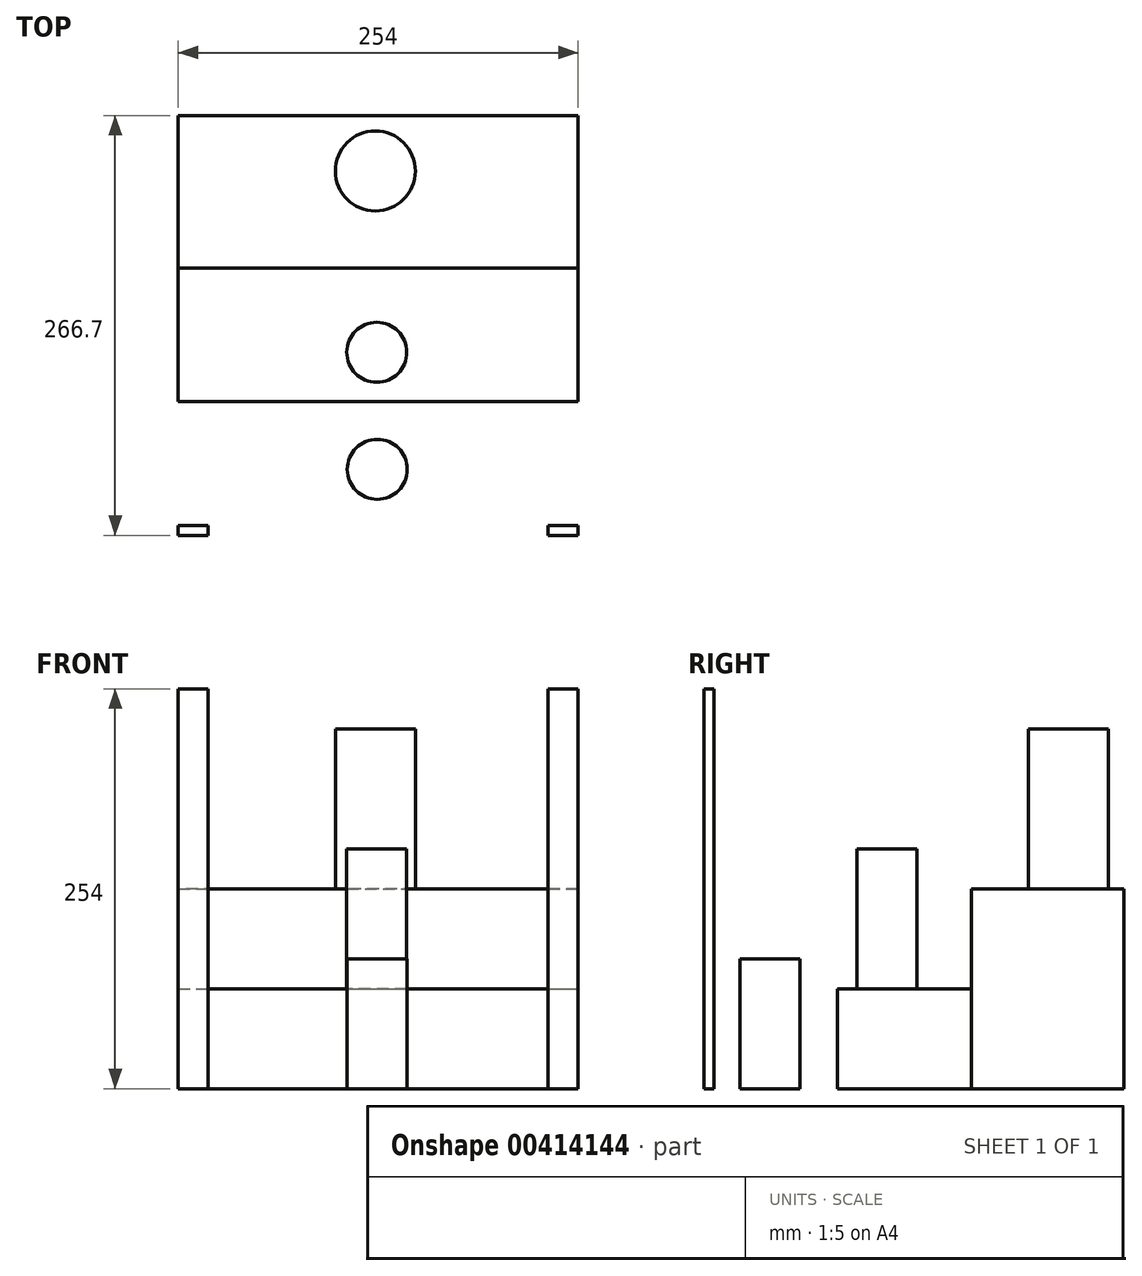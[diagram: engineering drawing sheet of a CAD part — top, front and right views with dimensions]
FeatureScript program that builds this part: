
annotation { "Feature Type Name" : "Feature", "Feature Type Description" : "" }
export const myFeature = defineFeature(function(context is Context, id is Id, definition is map)
    precondition{}
    {
        {
            var Q0;
            Q0=qCreatedBy(makeId("Front.planeOp"),FACE);
            cPlane(context, id + "F0", {"entities" : qUnion([Q0]), "cplaneType" : CPlaneType.OFFSET, "offset" : 266.7 * mm, "oppositeDirection" : true, "width" : 152.4 * mm, "height" : 152.4 * mm});
        }
        {
            var Q0;
            Q0=qCreatedBy(makeId("Right.planeOp"),FACE);
            cPlane(context, id + "F1", {"entities" : qUnion([Q0]), "cplaneType" : CPlaneType.OFFSET, "offset" : 254 * mm, "oppositeDirection" : true, "width" : 152.4 * mm, "height" : 152.4 * mm});
        }
        {
            var Q0;
            Q0=qCreatedBy(makeId("Top.planeOp"),FACE);
            cPlane(context, id + "F2", {"entities" : qUnion([Q0]), "cplaneType" : CPlaneType.OFFSET, "offset" : 254 * mm, "width" : 152.4 * mm, "height" : 152.4 * mm});
        }
        {
            var Q0;
            Q0=qCreatedBy(makeId("Front.planeOp"),FACE);
            var sketch = newSketch(context, id + "F3", { "sketchPlane" : qUnion([Q0])});
            skLineSegment(sketch, "E0", {"start": v(-254, 254) * mm, "end": v(-254, 0) * mm});
            skLineSegment(sketch, "E1", {"start": v(0, 254) * mm, "end": v(0, 0) * mm});
            skLineSegment(sketch, "E2", {"start": v(-254, 254) * mm, "end": v(0, 254) * mm});
            skLineSegment(sketch, "E3", {"start": v(-254, 0) * mm, "end": v(0, 0) * mm});
            skSolve(sketch);
        }
        {
            var Q0;
            Q0=makeQuery(id+"F3.imprint","IMPRINT",FACE,{"disambiguationData":[TD([[makeQuery(id+"F3.imprint","IMPRINT",EDGE,{"derivedFrom":sQuery(id+"F3.wireOp",EDGE,"E0")}),1.0]])]});
            var Q1;
            Q1=sQuery(id+"F3.wireOp",EDGE,"E1");
            var Q2;
            Q2=sQuery(id+"F3.wireOp",EDGE,"E2");
            var Q3;
            Q3=sQuery(id+"F3.wireOp",EDGE,"E0");
            var Q4;
            Q4=sQuery(id+"F3.wireOp",EDGE,"E3");
            var Q5;
            Q5=qCreatedBy(id+"F0.planeOp",FACE);
            extrude(context, id + "F4", {"entities" : qUnion([Q0]), "bodyType" : ToolBodyType.SURFACE, "surfaceEntities" : qUnion([Q1, Q2, Q3, Q4]), "endBound" : BoundingType.UP_TO_SURFACE, "oppositeDirection" : true, "endBoundEntityFace" : qUnion([Q5]), "depth" : 25.4 * mm});
        }
        {
            var Q0;
            Q0=qCreatedBy(makeId("Front.planeOp"),FACE);
            var sketch = newSketch(context, id + "F5", { "sketchPlane" : qUnion([Q0])});
            skLineSegment(sketch, "E4", {"start": v(-234.95, 254) * mm, "end": v(-234.95, 0) * mm});
            skLineSegment(sketch, "E5", {"start": v(-19.05, 254) * mm, "end": v(-19.05, 0) * mm});
            skLineSegment(sketch, "E6", {"start": v(-234.95, 254) * mm, "end": v(-254, 254) * mm});
            skLineSegment(sketch, "E7", {"start": v(-254, 254) * mm, "end": v(-254, 0) * mm});
            skLineSegment(sketch, "E8", {"start": v(-254, 0) * mm, "end": v(-234.95, 0) * mm});
            skLineSegment(sketch, "E9", {"start": v(-19.05, 254) * mm, "end": v(0, 254) * mm});
            skLineSegment(sketch, "E10", {"start": v(0, 254) * mm, "end": v(0, 0) * mm});
            skLineSegment(sketch, "E11", {"start": v(0, 0) * mm, "end": v(-19.05, 0) * mm});
            skSolve(sketch);
        }
        {
            var Q0;
            Q0=makeQuery(id+"F5.imprint","IMPRINT",FACE,{"disambiguationData":[TD([[makeQuery(id+"F5.imprint","IMPRINT",EDGE,{"derivedFrom":sQuery(id+"F5.wireOp",EDGE,"E4")}),-1.0]])]});
            var Q1;
            Q1=makeQuery(id+"F5.imprint","IMPRINT",FACE,{"disambiguationData":[TD([[makeQuery(id+"F5.imprint","IMPRINT",EDGE,{"derivedFrom":sQuery(id+"F5.wireOp",EDGE,"E5")}),1.0]])]});
            extrude(context, id + "F6", {"entities" : qUnion([Q0, Q1]), "oppositeDirection" : true, "depth" : 6.35 * mm});
        }
        {
            var Q0;
            Q0=makeQuery(id+"F4.opExtrude","SWEPT_FACE",FACE,{"disambiguationData":[OSD([sQuery(id+"F3.wireOp",EDGE,"E3")])]});
            var sketch = newSketch(context, id + "F7", { "sketchPlane" : qUnion([Q0])});
            skLineSegment(sketch, "E12", {"start": v(-254, 0) * mm, "end": v(0, 0) * mm});
            skLineSegment(sketch, "E13.1.0.0", {"start": v(-254, -84.84) * mm, "end": v(0, -84.84) * mm});
            skLineSegment(sketch, "E13.2.0.0", {"start": v(-254, -169.67) * mm, "end": v(0, -169.67) * mm});
            skLineSegment(sketch, "E13.direction1", {"start": v(-254, 0) * mm, "end": v(-254, -84.84) * mm, "construction": true});
            skLineSegment(sketch, "E14", {"start": v(-254, 0) * mm, "end": v(-254, -266.7) * mm});
            skLineSegment(sketch, "E15", {"start": v(-254, -266.7) * mm, "end": v(0, -266.7) * mm});
            skLineSegment(sketch, "E16", {"start": v(0, -266.7) * mm, "end": v(0, 0) * mm});
            skSolve(sketch);
        }
        {
            var Q0;
            {var subQ0=sQuery(id+"F7.wireOp",EDGE,"E13.1.0.0");Q0=makeQuery(id+"F7.imprint","IMPRINT",FACE,{"disambiguationData":[TD([[makeQuery(id+"F7.imprint","IMPRINT",EDGE,{"derivedFrom":subQ0}),-1.0]])]});}
            extrude(context, id + "F8", {"entities" : qUnion([Q0]), "oppositeDirection" : true, "depth" : 63.5 * mm});
        }
        {
            var Q0;
            {var subQ0=sQuery(id+"F7.wireOp",EDGE,"E13.2.0.0");Q0=makeQuery(id+"F7.imprint","IMPRINT",FACE,{"disambiguationData":[TD([[makeQuery(id+"F7.imprint","IMPRINT",EDGE,{"derivedFrom":subQ0}),-1.0]])]});}
            extrude(context, id + "F9", {"entities" : qUnion([Q0]), "oppositeDirection" : true, "depth" : 127 * mm});
        }
        {
            var Q0;
            {var subQ0=sQuery(id+"F7.wireOp",EDGE,"E12");Q0=makeQuery(id+"F7.imprint","IMPRINT",FACE,{"disambiguationData":[TD([[makeQuery(id+"F7.imprint","IMPRINT",EDGE,{"derivedFrom":subQ0}),1.0]])]});}
            var sketch = newSketch(context, id + "F10", { "sketchPlane" : qUnion([Q0])});
            skCircle(sketch, "E17", {"center": v(-127.6, -41.87) * mm, "radius": 19.05 * mm});
            skSolve(sketch);
        }
        {
            var Q0;
            Q0=makeQuery(id+"F10.imprint","IMPRINT",FACE,{"disambiguationData":[TD([[makeQuery(id+"F10.imprint","IMPRINT",EDGE,{"derivedFrom":sQuery(id+"F10.wireOp",EDGE,"E17")}),1.0]])]});
            var Q1;
            Q1=sQuery(id+"F10.wireOp",EDGE,"E17");
            extrude(context, id + "F11", {"entities" : qUnion([Q0]), "surfaceEntities" : qUnion([Q1]), "oppositeDirection" : true, "depth" : 82.55 * mm});
        }
        {
            var Q0;
            Q0=makeQuery(id+"F8.opExtrude","CAP_FACE",FACE,{"disambiguationData":[OSD([sQuery(id+"F7.wireOp",EDGE,"E13.1.0.0"),sQuery(id+"F7.wireOp",EDGE,"E13.2.0.0"),sQuery(id+"F7.wireOp",EDGE,"E14"),sQuery(id+"F7.wireOp",EDGE,"E16")])],"isStart":false});
            var sketch = newSketch(context, id + "F12", { "sketchPlane" : qUnion([Q0])});
            skCircle(sketch, "E18", {"center": v(-127.88, 116.25) * mm, "radius": 19.05 * mm});
            skSolve(sketch);
        }
        {
            var Q0;
            Q0=makeQuery(id+"F12.imprint","IMPRINT",FACE,{"disambiguationData":[TD([[makeQuery(id+"F12.imprint","IMPRINT",EDGE,{"derivedFrom":sQuery(id+"F12.wireOp",EDGE,"E18")}),1.0]])]});
            extrude(context, id + "F13", {"entities" : qUnion([Q0]), "operationType" : NewBodyOperationType.ADD, "depth" : 88.9 * mm});
        }
        {
            var Q0;
            Q0=makeQuery(id+"F9.opExtrude","CAP_FACE",FACE,{"disambiguationData":[OSD([sQuery(id+"F7.wireOp",EDGE,"E13.2.0.0"),sQuery(id+"F7.wireOp",EDGE,"E14"),sQuery(id+"F7.wireOp",EDGE,"E15"),sQuery(id+"F7.wireOp",EDGE,"E16")])],"isStart":false});
            var sketch = newSketch(context, id + "F14", { "sketchPlane" : qUnion([Q0])});
            skCircle(sketch, "E19", {"center": v(-128.8, 231.37) * mm, "radius": 25.4 * mm});
            skSolve(sketch);
        }
        {
            var Q0;
            Q0 = qSketchRegion(id + "F14", true);
            extrude(context, id + "F15", {"entities" : qUnion([Q0]), "operationType" : NewBodyOperationType.ADD, "depth" : 101.6 * mm});
        }
    });
